# Revit family: 0055312 Feilo Sylvania Lighting Fixture SYL-LAB LED IP65 REC 36W 4K OPAL 600 EB
name_source: partatom
category: Lighting Fixtures
revit_build: Autodesk Revit 2017 (Build: 20190507_1515(x64)
units: mm (PartAtom-declared; Revit-internal decimal feet)

## family parameters
Cut with Voids When Loaded = Yes
Host = Face
Light Source = Yes
OmniClass Number = 23.80.70.00
OmniClass Title = Lighting
Part Type = Normal
Room Calculation Point = No
Round Connector Dimension = Use Diameter
Shared = No

## types (1)
- 0055312 SYL-LAB LED IP65 REC 36W 4K OPAL 600 EB
    AccessoryMaterial = Trim-Sylvania-Syllab-Gray
    Apparent Load = 36 VA
    Assembly Code = D5020200
    AssetType = Fixed
    BodyMaterial = Body-Sylvania-Syllab-White
    ClassificationName = Uniclass2015
    ClassificationValue = EF_70_80
    Color Filter = 16777215
    Cost = 0 $
    Default Elevation = 1219 mm
    Description = IP65 Panel, dual IP65 (above and below), recessed for t-grid ceiling, CRI80, tamper proof, steel construction, opal plexiglass diffuser, 36W, 3950lm, 110lm/W, IK08, 4000K, 3 Step MacAdam Ellipse, driver current 800mA, Class 1, UGR<21, 220-240V, 50,000hrs (L70), HxWxD 595x595x105mm.
    DiffuserMaterial = Diffuser-Sylvania-Syllab-PC
    Dimming Lamp Color Temperature Shift = <None>
    DocumentationLiterature = http://www.sylvania-lighting.com
    DurationUnit = hours
    ElectricShockClassification = Class I
    Emit Shape Visible in Rendering = No
    Emit from Rectangle Length = 567 mm  [stored 1.86024 ft]
    Emit from Rectangle Width = 567 mm  [stored 1.86024 ft]
    ExpectedLife = 50000
    Height_FEILO = 105 mm  [stored 0.344488 ft]
    IfcExportAs = IfcLightFixtureType
    IfcExportType = IfcLightFixtureType
    ImpactProtectionIndex = IK08
    IngressProtection = IP65
    InputNominalFrequency = 50/60 Hz
    InputVoltage = 230-240V~
    Keynote = 16500
    Lamp = LED
    LampColourRenderingIndex = 80
    LampColourTemperature = 4000 K
    LampNominalLuminous = 3950 lm
    LampsType = LED
    LightOutputRatio = 100
    LuminousEfficacy = 109.7 lm/W
    Manufacturer = Feilo Sylvania
    ManufacturerName = Feilo Sylvania
    Material = steel housing, pmma (plexiglass) diffuser
    Model = SYL-LAB LED IP65 REC 36W 4K OPAL 600 EB
    ModelNumber = 0055312
    ModelReference = SYL-LAB LED IP65 REC 36W 4K OPAL 600 EB
    Name = SYL-LAB LED IP65 REC 36W 4K OPAL 600 EB
    NominalDepth = 595 mm  [stored 1.9521 ft]
    NominalHeight = 105 mm  [stored 0.344488 ft]
    NominalLength = 595 mm  [stored 1.9521 ft]
    Opal_FEILO = Yes
    Photometric Web File = 0055312.ies
    PowerConsumption = 36 W
    PowerFactor = 0.9
    ReflectorMaterial = <By Category>
    Reflector_FEILO = No
    Tilt Angle = -90.00°
    Type Image = <None>
    TypeName = SYL-LAB LED IP65 REC 36W 4K OPAL 600 EB
    URL = http://www.sylvania-lighting.com
    VisibilityBodyInner_FEILO = Yes
    VisibilityBodyUpperHD_FEILO = No
    VisibilityBodyUpper_FEILO = No
    VisibilityDiffuser_FEILO = Yes
    VisibilityTrim_FEILO = No
    Voltage = 230 V
    Weight = 8.5 kg

note: [stored X ft] marks values corroborated as IEEE doubles in the binary element streams (Revit-internal decimal feet)

## geometry (parser evidence)
native form markers: Sweep x4
no freeform markers — native parametric forms only
